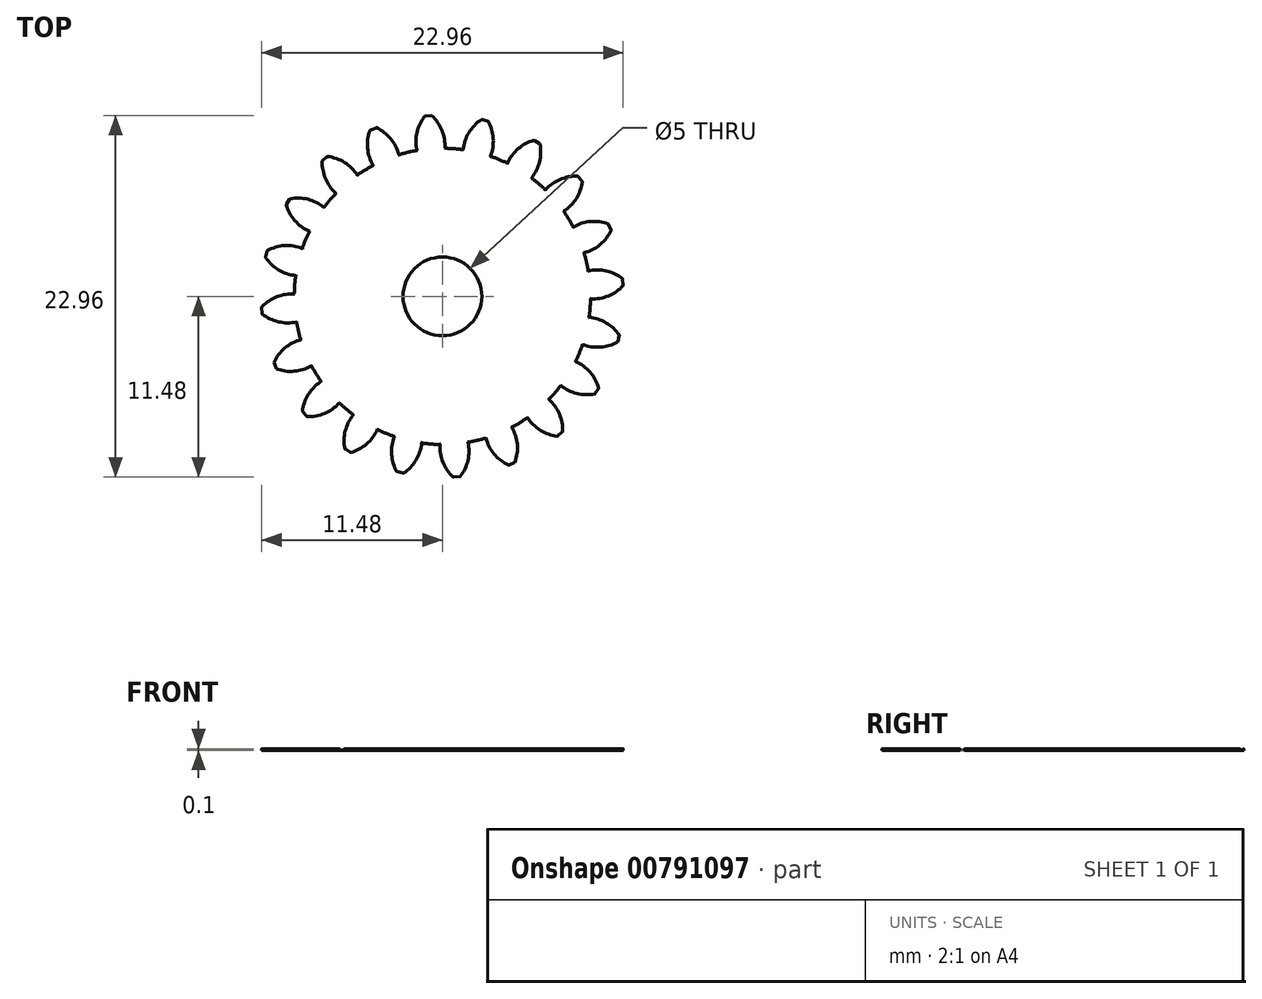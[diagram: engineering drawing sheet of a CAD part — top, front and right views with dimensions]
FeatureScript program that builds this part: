
annotation { "Feature Type Name" : "Feature", "Feature Type Description" : "" }
export const myFeature = defineFeature(function(context is Context, id is Id, definition is map)
    precondition{}
    {
        {
            assignVariable(context, id + "F0", {"name" : "GearDepth", "anyValue" : .1});
        }
        {
            assignVariable(context, id + "F1", {"name" : "TeethFillet", "anyValue" : getVariable(context, 'GearDepth') * .25});
        }
        {
            var Q0;
            Q0=qCreatedBy(makeId("Top.planeOp"),FACE);
            var sketch = newSketch(context, id + "F2", { "sketchPlane" : qUnion([Q0])});
            skCircle(sketch, "E0", {"center": v(0, 0) * mm, "radius": 9.4 * mm});
            skCircle(sketch, "E1", {"center": v(0, 0) * mm, "radius": 10.45 * mm, "construction": true});
            skCircle(sketch, "E2", {"center": v(0, 0) * mm, "radius": 11.5 * mm, "construction": true});
            skLineSegment(sketch, "E3", {"start": v(0, 0) * mm, "end": v(0, 17.6) * mm, "construction": true});
            skLineSegment(sketch, "E4", {"start": v(0, 0) * mm, "end": v(-1.42, 18) * mm, "construction": true});
            skLineSegment(sketch, "E5", {"start": v(0, 10.45) * mm, "end": v(-10.54, 10.45) * mm, "construction": true});
            skLineSegment(sketch, "E6", {"start": v(0, 10.45) * mm, "end": v(-10.3, 6.7) * mm, "construction": true});
            skCircle(sketch, "E7", {"center": v(0, 10.45) * mm, "radius": 2.61 * mm, "construction": true});
            skCircle(sketch, "E8", {"center": v(-2.46, 9.56) * mm, "radius": 2.61 * mm, "construction": true});
            skArc(sketch, "E9", {"start": v(-4.91, 10.45) * mm, "mid": v(-4.92, 10.42) * mm, "end": v(-4.94, 10.39) * mm});
            skArc(sketch, "E10.trimOffspring", {"start": v(0.15, 9.4) * mm, "mid": v(-0.03, 10.54) * mm, "end": v(-0.68, 11.48) * mm});
            skArc(sketch, "E11.MirrorCS", {"start": v(-1.62, 9.27) * mm, "mid": v(-1.62, 10.41) * mm, "end": v(-1.12, 11.45) * mm});
            skLineSegment(sketch, "E12", {"start": v(-1.12, 11.45) * mm, "end": v(-0.68, 11.48) * mm});
            skArc(sketch, "E13.1.0", {"start": v(-2.76, 9) * mm, "mid": v(-3.29, 10.01) * mm, "end": v(-4.2, 10.7) * mm});
            skLineSegment(sketch, "E13.1.1", {"start": v(-4.6, 10.54) * mm, "end": v(-4.2, 10.7) * mm});
            skArc(sketch, "E13.1.2", {"start": v(-4.4, 8.31) * mm, "mid": v(-4.76, 9.4) * mm, "end": v(-4.6, 10.54) * mm});
            skArc(sketch, "E13.2.0", {"start": v(-5.4, 7.7) * mm, "mid": v(-6.22, 8.5) * mm, "end": v(-7.3, 8.89) * mm});
            skLineSegment(sketch, "E13.2.1", {"start": v(-7.64, 8.6) * mm, "end": v(-7.3, 8.89) * mm});
            skArc(sketch, "E13.2.2", {"start": v(-6.76, 6.54) * mm, "mid": v(-7.43, 7.47) * mm, "end": v(-7.64, 8.6) * mm});
            skArc(sketch, "E13.3.0", {"start": v(-7.52, 5.65) * mm, "mid": v(-8.54, 6.17) * mm, "end": v(-9.69, 6.2) * mm});
            skLineSegment(sketch, "E13.3.1", {"start": v(-9.92, 5.82) * mm, "end": v(-9.69, 6.2) * mm});
            skArc(sketch, "E13.3.2", {"start": v(-8.45, 4.13) * mm, "mid": v(-9.37, 4.81) * mm, "end": v(-9.92, 5.82) * mm});
            skArc(sketch, "E13.4.0", {"start": v(-8.9, 3.05) * mm, "mid": v(-10.03, 3.23) * mm, "end": v(-11.13, 2.9) * mm});
            skLineSegment(sketch, "E13.4.1", {"start": v(-11.23, 2.47) * mm, "end": v(-11.13, 2.9) * mm});
            skArc(sketch, "E13.4.2", {"start": v(-9.32, 1.32) * mm, "mid": v(-10.4, 1.68) * mm, "end": v(-11.23, 2.47) * mm});
            skArc(sketch, "E13.5.0", {"start": v(-9.4, 0.15) * mm, "mid": v(-10.54, -0.03) * mm, "end": v(-11.48, -0.68) * mm});
            skLineSegment(sketch, "E13.5.1", {"start": v(-11.45, -1.12) * mm, "end": v(-11.48, -0.68) * mm});
            skArc(sketch, "E13.5.2", {"start": v(-9.27, -1.62) * mm, "mid": v(-10.41, -1.62) * mm, "end": v(-11.45, -1.12) * mm});
            skArc(sketch, "E13.6.0", {"start": v(-9, -2.76) * mm, "mid": v(-10.01, -3.29) * mm, "end": v(-10.7, -4.2) * mm});
            skLineSegment(sketch, "E13.6.1", {"start": v(-10.54, -4.6) * mm, "end": v(-10.7, -4.2) * mm});
            skArc(sketch, "E13.6.2", {"start": v(-8.31, -4.4) * mm, "mid": v(-9.4, -4.76) * mm, "end": v(-10.54, -4.6) * mm});
            skArc(sketch, "E13.7.0", {"start": v(-7.7, -5.4) * mm, "mid": v(-8.5, -6.22) * mm, "end": v(-8.89, -7.3) * mm});
            skLineSegment(sketch, "E13.7.1", {"start": v(-8.6, -7.64) * mm, "end": v(-8.89, -7.3) * mm});
            skArc(sketch, "E13.7.2", {"start": v(-6.54, -6.76) * mm, "mid": v(-7.47, -7.43) * mm, "end": v(-8.6, -7.64) * mm});
            skArc(sketch, "E13.8.0", {"start": v(-5.65, -7.52) * mm, "mid": v(-6.17, -8.54) * mm, "end": v(-6.2, -9.69) * mm});
            skLineSegment(sketch, "E13.8.1", {"start": v(-5.82, -9.92) * mm, "end": v(-6.2, -9.69) * mm});
            skArc(sketch, "E13.8.2", {"start": v(-4.13, -8.45) * mm, "mid": v(-4.81, -9.37) * mm, "end": v(-5.82, -9.92) * mm});
            skArc(sketch, "E13.9.0", {"start": v(-3.05, -8.9) * mm, "mid": v(-3.23, -10.03) * mm, "end": v(-2.9, -11.13) * mm});
            skLineSegment(sketch, "E13.9.1", {"start": v(-2.47, -11.23) * mm, "end": v(-2.9, -11.13) * mm});
            skArc(sketch, "E13.9.2", {"start": v(-1.32, -9.32) * mm, "mid": v(-1.68, -10.4) * mm, "end": v(-2.47, -11.23) * mm});
            skArc(sketch, "E13.10.0", {"start": v(-0.15, -9.4) * mm, "mid": v(0.03, -10.54) * mm, "end": v(0.68, -11.48) * mm});
            skLineSegment(sketch, "E13.10.1", {"start": v(1.12, -11.45) * mm, "end": v(0.68, -11.48) * mm});
            skArc(sketch, "E13.10.2", {"start": v(1.62, -9.27) * mm, "mid": v(1.62, -10.41) * mm, "end": v(1.12, -11.45) * mm});
            skArc(sketch, "E13.11.0", {"start": v(2.76, -9) * mm, "mid": v(3.29, -10.01) * mm, "end": v(4.2, -10.7) * mm});
            skLineSegment(sketch, "E13.11.1", {"start": v(4.6, -10.54) * mm, "end": v(4.2, -10.7) * mm});
            skArc(sketch, "E13.11.2", {"start": v(4.4, -8.31) * mm, "mid": v(4.76, -9.4) * mm, "end": v(4.6, -10.54) * mm});
            skArc(sketch, "E13.12.0", {"start": v(5.4, -7.7) * mm, "mid": v(6.22, -8.5) * mm, "end": v(7.3, -8.89) * mm});
            skLineSegment(sketch, "E13.12.1", {"start": v(7.64, -8.6) * mm, "end": v(7.3, -8.89) * mm});
            skArc(sketch, "E13.12.2", {"start": v(6.76, -6.54) * mm, "mid": v(7.43, -7.47) * mm, "end": v(7.64, -8.6) * mm});
            skArc(sketch, "E13.13.0", {"start": v(7.52, -5.65) * mm, "mid": v(8.54, -6.17) * mm, "end": v(9.69, -6.2) * mm});
            skLineSegment(sketch, "E13.13.1", {"start": v(9.92, -5.82) * mm, "end": v(9.69, -6.2) * mm});
            skArc(sketch, "E13.13.2", {"start": v(8.45, -4.13) * mm, "mid": v(9.37, -4.81) * mm, "end": v(9.92, -5.82) * mm});
            skArc(sketch, "E13.14.0", {"start": v(8.9, -3.05) * mm, "mid": v(10.03, -3.23) * mm, "end": v(11.13, -2.9) * mm});
            skLineSegment(sketch, "E13.14.1", {"start": v(11.23, -2.47) * mm, "end": v(11.13, -2.9) * mm});
            skArc(sketch, "E13.14.2", {"start": v(9.32, -1.32) * mm, "mid": v(10.4, -1.68) * mm, "end": v(11.23, -2.47) * mm});
            skArc(sketch, "E13.15.0", {"start": v(9.4, -0.15) * mm, "mid": v(10.54, 0.03) * mm, "end": v(11.48, 0.68) * mm});
            skLineSegment(sketch, "E13.15.1", {"start": v(11.45, 1.12) * mm, "end": v(11.48, 0.68) * mm});
            skArc(sketch, "E13.15.2", {"start": v(9.27, 1.62) * mm, "mid": v(10.41, 1.62) * mm, "end": v(11.45, 1.12) * mm});
            skArc(sketch, "E13.16.0", {"start": v(9, 2.76) * mm, "mid": v(10.01, 3.29) * mm, "end": v(10.7, 4.2) * mm});
            skLineSegment(sketch, "E13.16.1", {"start": v(10.54, 4.6) * mm, "end": v(10.7, 4.2) * mm});
            skArc(sketch, "E13.16.2", {"start": v(8.31, 4.4) * mm, "mid": v(9.4, 4.76) * mm, "end": v(10.54, 4.6) * mm});
            skArc(sketch, "E13.17.0", {"start": v(7.7, 5.4) * mm, "mid": v(8.5, 6.22) * mm, "end": v(8.89, 7.3) * mm});
            skLineSegment(sketch, "E13.17.1", {"start": v(8.6, 7.64) * mm, "end": v(8.89, 7.3) * mm});
            skArc(sketch, "E13.17.2", {"start": v(6.54, 6.76) * mm, "mid": v(7.47, 7.43) * mm, "end": v(8.6, 7.64) * mm});
            skArc(sketch, "E13.18.0", {"start": v(5.65, 7.52) * mm, "mid": v(6.17, 8.54) * mm, "end": v(6.2, 9.69) * mm});
            skLineSegment(sketch, "E13.18.1", {"start": v(5.82, 9.92) * mm, "end": v(6.2, 9.69) * mm});
            skArc(sketch, "E13.18.2", {"start": v(4.13, 8.45) * mm, "mid": v(4.81, 9.37) * mm, "end": v(5.82, 9.92) * mm});
            skArc(sketch, "E13.19.0", {"start": v(3.05, 8.9) * mm, "mid": v(3.23, 10.03) * mm, "end": v(2.9, 11.13) * mm});
            skLineSegment(sketch, "E13.19.1", {"start": v(2.47, 11.23) * mm, "end": v(2.9, 11.13) * mm});
            skArc(sketch, "E13.19.2", {"start": v(1.32, 9.32) * mm, "mid": v(1.68, 10.4) * mm, "end": v(2.47, 11.23) * mm});
            skCircle(sketch, "E14", {"center": v(0, 0) * mm, "radius": 2.5 * mm});
            skSolve(sketch);
        }
        {
            var Q0;
            {var subQ0=sQuery(id+"F2.wireOp",EDGE,"E10.trimOffspring");Q0=makeQuery(id+"F2.imprint","IMPRINT",FACE,{"disambiguationData":[TD([[makeQuery(id+"F2.imprint","IMPRINT",EDGE,{"derivedFrom":subQ0}),1.0]])]});}
            var Q1;
            {var subQ0=sQuery(id+"F2.wireOp",EDGE,"E0");var subQ1=makeQuery(id+"F2.imprint","INTERSECT",VERTEX,{"derivedFrom":[subQ0,sQuery(id+"F2.wireOp",EDGE,"E10.trimOffspring")]});Q1=makeQuery(id+"F2.imprint","IMPRINT",FACE,{"disambiguationData":[TD([[makeQuery(id+"F2.imprint","IMPRINT",EDGE,{"disambiguationData":[TD([[subQ1,-1.0]])],"derivedFrom":subQ0}),1.0]])]});}
            var Q2;
            {var subQ0=sQuery(id+"F2.wireOp",EDGE,"E13.1.0");Q2=makeQuery(id+"F2.imprint","IMPRINT",FACE,{"disambiguationData":[TD([[makeQuery(id+"F2.imprint","IMPRINT",EDGE,{"derivedFrom":subQ0}),1.0]])]});}
            var Q3;
            {var subQ0=sQuery(id+"F2.wireOp",EDGE,"E13.2.0");Q3=makeQuery(id+"F2.imprint","IMPRINT",FACE,{"disambiguationData":[TD([[makeQuery(id+"F2.imprint","IMPRINT",EDGE,{"derivedFrom":subQ0}),1.0]])]});}
            var Q4;
            {var subQ0=sQuery(id+"F2.wireOp",EDGE,"E13.3.0");Q4=makeQuery(id+"F2.imprint","IMPRINT",FACE,{"disambiguationData":[TD([[makeQuery(id+"F2.imprint","IMPRINT",EDGE,{"derivedFrom":subQ0}),1.0]])]});}
            var Q5;
            {var subQ0=sQuery(id+"F2.wireOp",EDGE,"E13.4.0");Q5=makeQuery(id+"F2.imprint","IMPRINT",FACE,{"disambiguationData":[TD([[makeQuery(id+"F2.imprint","IMPRINT",EDGE,{"derivedFrom":subQ0}),1.0]])]});}
            var Q6;
            {var subQ0=sQuery(id+"F2.wireOp",EDGE,"E13.5.0");Q6=makeQuery(id+"F2.imprint","IMPRINT",FACE,{"disambiguationData":[TD([[makeQuery(id+"F2.imprint","IMPRINT",EDGE,{"derivedFrom":subQ0}),1.0]])]});}
            var Q7;
            {var subQ0=sQuery(id+"F2.wireOp",EDGE,"E13.6.0");Q7=makeQuery(id+"F2.imprint","IMPRINT",FACE,{"disambiguationData":[TD([[makeQuery(id+"F2.imprint","IMPRINT",EDGE,{"derivedFrom":subQ0}),1.0]])]});}
            var Q8;
            {var subQ0=sQuery(id+"F2.wireOp",EDGE,"E13.7.0");Q8=makeQuery(id+"F2.imprint","IMPRINT",FACE,{"disambiguationData":[TD([[makeQuery(id+"F2.imprint","IMPRINT",EDGE,{"derivedFrom":subQ0}),1.0]])]});}
            var Q9;
            {var subQ0=sQuery(id+"F2.wireOp",EDGE,"E13.8.0");Q9=makeQuery(id+"F2.imprint","IMPRINT",FACE,{"disambiguationData":[TD([[makeQuery(id+"F2.imprint","IMPRINT",EDGE,{"derivedFrom":subQ0}),1.0]])]});}
            var Q10;
            {var subQ0=sQuery(id+"F2.wireOp",EDGE,"E13.9.0");Q10=makeQuery(id+"F2.imprint","IMPRINT",FACE,{"disambiguationData":[TD([[makeQuery(id+"F2.imprint","IMPRINT",EDGE,{"derivedFrom":subQ0}),1.0]])]});}
            var Q11;
            {var subQ0=sQuery(id+"F2.wireOp",EDGE,"E13.10.0");Q11=makeQuery(id+"F2.imprint","IMPRINT",FACE,{"disambiguationData":[TD([[makeQuery(id+"F2.imprint","IMPRINT",EDGE,{"derivedFrom":subQ0}),1.0]])]});}
            var Q12;
            {var subQ0=sQuery(id+"F2.wireOp",EDGE,"E13.11.0");Q12=makeQuery(id+"F2.imprint","IMPRINT",FACE,{"disambiguationData":[TD([[makeQuery(id+"F2.imprint","IMPRINT",EDGE,{"derivedFrom":subQ0}),1.0]])]});}
            var Q13;
            {var subQ0=sQuery(id+"F2.wireOp",EDGE,"E13.12.0");Q13=makeQuery(id+"F2.imprint","IMPRINT",FACE,{"disambiguationData":[TD([[makeQuery(id+"F2.imprint","IMPRINT",EDGE,{"derivedFrom":subQ0}),1.0]])]});}
            var Q14;
            {var subQ0=sQuery(id+"F2.wireOp",EDGE,"E13.13.0");Q14=makeQuery(id+"F2.imprint","IMPRINT",FACE,{"disambiguationData":[TD([[makeQuery(id+"F2.imprint","IMPRINT",EDGE,{"derivedFrom":subQ0}),1.0]])]});}
            var Q15;
            {var subQ0=sQuery(id+"F2.wireOp",EDGE,"E13.14.0");Q15=makeQuery(id+"F2.imprint","IMPRINT",FACE,{"disambiguationData":[TD([[makeQuery(id+"F2.imprint","IMPRINT",EDGE,{"derivedFrom":subQ0}),1.0]])]});}
            var Q16;
            {var subQ0=sQuery(id+"F2.wireOp",EDGE,"E13.15.0");Q16=makeQuery(id+"F2.imprint","IMPRINT",FACE,{"disambiguationData":[TD([[makeQuery(id+"F2.imprint","IMPRINT",EDGE,{"derivedFrom":subQ0}),1.0]])]});}
            var Q17;
            {var subQ0=sQuery(id+"F2.wireOp",EDGE,"E13.16.0");Q17=makeQuery(id+"F2.imprint","IMPRINT",FACE,{"disambiguationData":[TD([[makeQuery(id+"F2.imprint","IMPRINT",EDGE,{"derivedFrom":subQ0}),1.0]])]});}
            var Q18;
            {var subQ0=sQuery(id+"F2.wireOp",EDGE,"E13.17.0");Q18=makeQuery(id+"F2.imprint","IMPRINT",FACE,{"disambiguationData":[TD([[makeQuery(id+"F2.imprint","IMPRINT",EDGE,{"derivedFrom":subQ0}),1.0]])]});}
            var Q19;
            {var subQ0=sQuery(id+"F2.wireOp",EDGE,"E13.18.0");Q19=makeQuery(id+"F2.imprint","IMPRINT",FACE,{"disambiguationData":[TD([[makeQuery(id+"F2.imprint","IMPRINT",EDGE,{"derivedFrom":subQ0}),1.0]])]});}
            var Q20;
            {var subQ0=sQuery(id+"F2.wireOp",EDGE,"E13.19.0");Q20=makeQuery(id+"F2.imprint","IMPRINT",FACE,{"disambiguationData":[TD([[makeQuery(id+"F2.imprint","IMPRINT",EDGE,{"derivedFrom":subQ0}),1.0]])]});}
            var Q21;
            Q21=sQuery(id+"F2.wireOp",EDGE,"E0");
            var Q22;
            Q22=sQuery(id+"F2.wireOp",EDGE,"E10.trimOffspring");
            var Q23;
            Q23=sQuery(id+"F2.wireOp",EDGE,"E12");
            var Q24;
            Q24=sQuery(id+"F2.wireOp",EDGE,"E11.MirrorCS");
            extrude(context, id + "F3", {"entities" : qUnion([Q0, Q1, Q2, Q3, Q4, Q5, Q6, Q7, Q8, Q9, Q10, Q11, Q12, Q13, Q14, Q15, Q16, Q17, Q18, Q19, Q20]), "surfaceEntities" : qUnion([Q21, Q22, Q23, Q24]), "depth" : (getVariable(context, 'GearDepth')) * mm});
        }
        {
            var Q0;
            Q0=makeQuery(id+"F3.opExtrude","CAP_EDGE",EDGE,{"disambiguationData":[OSD([sQuery(id+"F2.wireOp",EDGE,"E13.5.2")])],"isStart":false});
            var Q1;
            Q1=makeQuery(id+"F3.opExtrude","CAP_EDGE",EDGE,{"disambiguationData":[OSD([sQuery(id+"F2.wireOp",EDGE,"E13.5.1")])],"isStart":false});
            var Q2;
            {var subQ0=sQuery(id+"F2.wireOp",EDGE,"E0");Q2=makeQuery(id+"F3.opExtrude","CAP_EDGE",EDGE,{"disambiguationData":[OSD([subQ0]),TDD([makeQuery(id+"F2.imprint","IMPRINT",EDGE,{"disambiguationData":[TD([[makeQuery(id+"F2.imprint","INTERSECT",VERTEX,{"derivedFrom":[subQ0,sQuery(id+"F2.wireOp",EDGE,"E13.5.2")]}),-1.0]])],"derivedFrom":subQ0})])],"isStart":false});}
            var Q3;
            Q3=makeQuery(id+"F3.opExtrude","CAP_EDGE",EDGE,{"disambiguationData":[OSD([sQuery(id+"F2.wireOp",EDGE,"E13.6.0")])],"isStart":false});
            var Q4;
            Q4=makeQuery(id+"F3.opExtrude","CAP_EDGE",EDGE,{"disambiguationData":[OSD([sQuery(id+"F2.wireOp",EDGE,"E13.6.1")])],"isStart":false});
            var Q5;
            Q5=makeQuery(id+"F3.opExtrude","CAP_EDGE",EDGE,{"disambiguationData":[OSD([sQuery(id+"F2.wireOp",EDGE,"E13.6.2")])],"isStart":false});
            var Q6;
            {var subQ0=sQuery(id+"F2.wireOp",EDGE,"E0");Q6=makeQuery(id+"F3.opExtrude","SWEPT_FACE",FACE,{"disambiguationData":[OSD([subQ0]),TDD([makeQuery(id+"F2.imprint","IMPRINT",EDGE,{"disambiguationData":[TD([[makeQuery(id+"F2.imprint","INTERSECT",VERTEX,{"derivedFrom":[subQ0,sQuery(id+"F2.wireOp",EDGE,"E13.6.2")]}),-1.0]])],"derivedFrom":subQ0})])]});}
            var Q7;
            {var subQ0=sQuery(id+"F2.wireOp",EDGE,"E0");Q7=makeQuery(id+"F3.opExtrude","CAP_EDGE",EDGE,{"disambiguationData":[OSD([subQ0]),TDD([makeQuery(id+"F2.imprint","IMPRINT",EDGE,{"disambiguationData":[TD([[makeQuery(id+"F2.imprint","INTERSECT",VERTEX,{"derivedFrom":[subQ0,sQuery(id+"F2.wireOp",EDGE,"E13.6.2")]}),-1.0]])],"derivedFrom":subQ0})])],"isStart":false});}
            var Q8;
            Q8=makeQuery(id+"F3.opExtrude","CAP_EDGE",EDGE,{"disambiguationData":[OSD([sQuery(id+"F2.wireOp",EDGE,"E13.7.2")])],"isStart":true});
            var Q9;
            {var subQ0=sQuery(id+"F2.wireOp",EDGE,"E0");Q9=makeQuery(id+"F3.opExtrude","CAP_EDGE",EDGE,{"disambiguationData":[OSD([subQ0]),TDD([makeQuery(id+"F2.imprint","IMPRINT",EDGE,{"disambiguationData":[TD([[makeQuery(id+"F2.imprint","INTERSECT",VERTEX,{"derivedFrom":[subQ0,sQuery(id+"F2.wireOp",EDGE,"E13.7.2")]}),-1.0]])],"derivedFrom":subQ0})])],"isStart":true});}
            var Q10;
            Q10=makeQuery(id+"F3.opExtrude","CAP_EDGE",EDGE,{"disambiguationData":[OSD([sQuery(id+"F2.wireOp",EDGE,"E13.7.2")])],"isStart":false});
            var Q11;
            {var subQ0=sQuery(id+"F2.wireOp",EDGE,"E0");Q11=makeQuery(id+"F3.opExtrude","CAP_EDGE",EDGE,{"disambiguationData":[OSD([subQ0]),TDD([makeQuery(id+"F2.imprint","IMPRINT",EDGE,{"disambiguationData":[TD([[makeQuery(id+"F2.imprint","INTERSECT",VERTEX,{"derivedFrom":[subQ0,sQuery(id+"F2.wireOp",EDGE,"E13.7.2")]}),-1.0]])],"derivedFrom":subQ0})])],"isStart":false});}
            var Q12;
            Q12=makeQuery(id+"F3.opExtrude","CAP_EDGE",EDGE,{"disambiguationData":[OSD([sQuery(id+"F2.wireOp",EDGE,"E13.8.0")])],"isStart":false});
            var Q13;
            {var subQ0=sQuery(id+"F2.wireOp",EDGE,"E0");Q13=makeQuery(id+"F3.opExtrude","SWEPT_FACE",FACE,{"disambiguationData":[OSD([subQ0]),TDD([makeQuery(id+"F2.imprint","IMPRINT",EDGE,{"disambiguationData":[TD([[makeQuery(id+"F2.imprint","INTERSECT",VERTEX,{"derivedFrom":[subQ0,sQuery(id+"F2.wireOp",EDGE,"E13.7.2")]}),-1.0]])],"derivedFrom":subQ0})])]});}
            var Q14;
            Q14=makeQuery(id+"F3.opExtrude","CAP_EDGE",EDGE,{"disambiguationData":[OSD([sQuery(id+"F2.wireOp",EDGE,"E13.6.0")])],"isStart":true});
            var Q15;
            Q15=makeQuery(id+"F3.opExtrude","CAP_EDGE",EDGE,{"disambiguationData":[OSD([sQuery(id+"F2.wireOp",EDGE,"E13.8.2")])],"isStart":false});
            var Q16;
            {var subQ0=sQuery(id+"F2.wireOp",EDGE,"E0");Q16=makeQuery(id+"F3.opExtrude","CAP_EDGE",EDGE,{"disambiguationData":[OSD([subQ0]),TDD([makeQuery(id+"F2.imprint","IMPRINT",EDGE,{"disambiguationData":[TD([[makeQuery(id+"F2.imprint","INTERSECT",VERTEX,{"derivedFrom":[subQ0,sQuery(id+"F2.wireOp",EDGE,"E13.8.2")]}),-1.0]])],"derivedFrom":subQ0})])],"isStart":false});}
            var Q17;
            Q17=makeQuery(id+"F3.opExtrude","CAP_EDGE",EDGE,{"disambiguationData":[OSD([sQuery(id+"F2.wireOp",EDGE,"E13.9.0")])],"isStart":false});
            var Q18;
            Q18=makeQuery(id+"F3.opExtrude","CAP_EDGE",EDGE,{"disambiguationData":[OSD([sQuery(id+"F2.wireOp",EDGE,"E13.9.2")])],"isStart":false});
            var Q19;
            {var subQ0=sQuery(id+"F2.wireOp",EDGE,"E0");Q19=makeQuery(id+"F3.opExtrude","CAP_EDGE",EDGE,{"disambiguationData":[OSD([subQ0]),TDD([makeQuery(id+"F2.imprint","IMPRINT",EDGE,{"disambiguationData":[TD([[makeQuery(id+"F2.imprint","INTERSECT",VERTEX,{"derivedFrom":[subQ0,sQuery(id+"F2.wireOp",EDGE,"E13.9.2")]}),-1.0]])],"derivedFrom":subQ0})])],"isStart":false});}
            var Q20;
            Q20=makeQuery(id+"F3.opExtrude","CAP_EDGE",EDGE,{"disambiguationData":[OSD([sQuery(id+"F2.wireOp",EDGE,"E13.10.0")])],"isStart":false});
            var Q21;
            Q21=makeQuery(id+"F3.opExtrude","CAP_EDGE",EDGE,{"disambiguationData":[OSD([sQuery(id+"F2.wireOp",EDGE,"E13.10.2")])],"isStart":false});
            var Q22;
            {var subQ0=sQuery(id+"F2.wireOp",EDGE,"E0");Q22=makeQuery(id+"F3.opExtrude","CAP_EDGE",EDGE,{"disambiguationData":[OSD([subQ0]),TDD([makeQuery(id+"F2.imprint","IMPRINT",EDGE,{"disambiguationData":[TD([[makeQuery(id+"F2.imprint","INTERSECT",VERTEX,{"derivedFrom":[subQ0,sQuery(id+"F2.wireOp",EDGE,"E13.10.2")]}),-1.0]])],"derivedFrom":subQ0})])],"isStart":false});}
            var Q23;
            Q23=makeQuery(id+"F3.opExtrude","CAP_EDGE",EDGE,{"disambiguationData":[OSD([sQuery(id+"F2.wireOp",EDGE,"E13.11.0")])],"isStart":false});
            var Q24;
            Q24=makeQuery(id+"F3.opExtrude","CAP_EDGE",EDGE,{"disambiguationData":[OSD([sQuery(id+"F2.wireOp",EDGE,"E13.11.2")])],"isStart":false});
            var Q25;
            {var subQ0=sQuery(id+"F2.wireOp",EDGE,"E0");Q25=makeQuery(id+"F3.opExtrude","CAP_EDGE",EDGE,{"disambiguationData":[OSD([subQ0]),TDD([makeQuery(id+"F2.imprint","IMPRINT",EDGE,{"disambiguationData":[TD([[makeQuery(id+"F2.imprint","INTERSECT",VERTEX,{"derivedFrom":[subQ0,sQuery(id+"F2.wireOp",EDGE,"E13.11.2")]}),-1.0]])],"derivedFrom":subQ0})])],"isStart":false});}
            var Q26;
            Q26=makeQuery(id+"F3.opExtrude","CAP_EDGE",EDGE,{"disambiguationData":[OSD([sQuery(id+"F2.wireOp",EDGE,"E13.12.0")])],"isStart":false});
            var Q27;
            Q27=makeQuery(id+"F3.opExtrude","CAP_EDGE",EDGE,{"disambiguationData":[OSD([sQuery(id+"F2.wireOp",EDGE,"E13.12.2")])],"isStart":false});
            var Q28;
            {var subQ0=sQuery(id+"F2.wireOp",EDGE,"E0");Q28=makeQuery(id+"F3.opExtrude","CAP_EDGE",EDGE,{"disambiguationData":[OSD([subQ0]),TDD([makeQuery(id+"F2.imprint","IMPRINT",EDGE,{"disambiguationData":[TD([[makeQuery(id+"F2.imprint","INTERSECT",VERTEX,{"derivedFrom":[subQ0,sQuery(id+"F2.wireOp",EDGE,"E13.12.2")]}),-1.0]])],"derivedFrom":subQ0})])],"isStart":false});}
            var Q29;
            Q29=makeQuery(id+"F3.opExtrude","CAP_EDGE",EDGE,{"disambiguationData":[OSD([sQuery(id+"F2.wireOp",EDGE,"E13.13.0")])],"isStart":false});
            var Q30;
            Q30=makeQuery(id+"F3.opExtrude","CAP_EDGE",EDGE,{"disambiguationData":[OSD([sQuery(id+"F2.wireOp",EDGE,"E13.13.2")])],"isStart":false});
            var Q31;
            {var subQ0=sQuery(id+"F2.wireOp",EDGE,"E0");Q31=makeQuery(id+"F3.opExtrude","CAP_EDGE",EDGE,{"disambiguationData":[OSD([subQ0]),TDD([makeQuery(id+"F2.imprint","IMPRINT",EDGE,{"disambiguationData":[TD([[makeQuery(id+"F2.imprint","INTERSECT",VERTEX,{"derivedFrom":[subQ0,sQuery(id+"F2.wireOp",EDGE,"E13.13.2")]}),-1.0]])],"derivedFrom":subQ0})])],"isStart":false});}
            var Q32;
            Q32=makeQuery(id+"F3.opExtrude","CAP_EDGE",EDGE,{"disambiguationData":[OSD([sQuery(id+"F2.wireOp",EDGE,"E13.14.0")])],"isStart":false});
            var Q33;
            Q33=makeQuery(id+"F3.opExtrude","CAP_EDGE",EDGE,{"disambiguationData":[OSD([sQuery(id+"F2.wireOp",EDGE,"E13.14.2")])],"isStart":false});
            var Q34;
            {var subQ0=sQuery(id+"F2.wireOp",EDGE,"E0");Q34=makeQuery(id+"F3.opExtrude","CAP_EDGE",EDGE,{"disambiguationData":[OSD([subQ0]),TDD([makeQuery(id+"F2.imprint","IMPRINT",EDGE,{"disambiguationData":[TD([[makeQuery(id+"F2.imprint","INTERSECT",VERTEX,{"derivedFrom":[subQ0,sQuery(id+"F2.wireOp",EDGE,"E13.14.2")]}),-1.0]])],"derivedFrom":subQ0})])],"isStart":false});}
            var Q35;
            Q35=makeQuery(id+"F3.opExtrude","CAP_EDGE",EDGE,{"disambiguationData":[OSD([sQuery(id+"F2.wireOp",EDGE,"E13.15.0")])],"isStart":false});
            var Q36;
            {var subQ0=sQuery(id+"F2.wireOp",EDGE,"E0");Q36=makeQuery(id+"F3.opExtrude","CAP_EDGE",EDGE,{"disambiguationData":[OSD([subQ0]),TDD([makeQuery(id+"F2.imprint","IMPRINT",EDGE,{"disambiguationData":[TD([[makeQuery(id+"F2.imprint","INTERSECT",VERTEX,{"derivedFrom":[subQ0,sQuery(id+"F2.wireOp",EDGE,"E13.14.2")]}),-1.0]])],"derivedFrom":subQ0})])],"isStart":false});}
            var Q37;
            Q37=makeQuery(id+"F3.opExtrude","CAP_EDGE",EDGE,{"disambiguationData":[OSD([sQuery(id+"F2.wireOp",EDGE,"E13.15.2")])],"isStart":false});
            var Q38;
            {var subQ0=sQuery(id+"F2.wireOp",EDGE,"E0");Q38=makeQuery(id+"F3.opExtrude","CAP_EDGE",EDGE,{"disambiguationData":[OSD([subQ0]),TDD([makeQuery(id+"F2.imprint","IMPRINT",EDGE,{"disambiguationData":[TD([[makeQuery(id+"F2.imprint","INTERSECT",VERTEX,{"derivedFrom":[subQ0,sQuery(id+"F2.wireOp",EDGE,"E13.15.2")]}),-1.0]])],"derivedFrom":subQ0})])],"isStart":false});}
            var Q39;
            Q39=makeQuery(id+"F3.opExtrude","CAP_EDGE",EDGE,{"disambiguationData":[OSD([sQuery(id+"F2.wireOp",EDGE,"E13.16.0")])],"isStart":false});
            var Q40;
            Q40=makeQuery(id+"F3.opExtrude","CAP_EDGE",EDGE,{"disambiguationData":[OSD([sQuery(id+"F2.wireOp",EDGE,"E13.16.2")])],"isStart":false});
            var Q41;
            Q41=makeQuery(id+"F3.opExtrude","CAP_EDGE",EDGE,{"disambiguationData":[OSD([sQuery(id+"F2.wireOp",EDGE,"E13.17.0")])],"isStart":false});
            var Q42;
            {var subQ0=sQuery(id+"F2.wireOp",EDGE,"E0");Q42=makeQuery(id+"F3.opExtrude","CAP_EDGE",EDGE,{"disambiguationData":[OSD([subQ0]),TDD([makeQuery(id+"F2.imprint","IMPRINT",EDGE,{"disambiguationData":[TD([[makeQuery(id+"F2.imprint","INTERSECT",VERTEX,{"derivedFrom":[subQ0,sQuery(id+"F2.wireOp",EDGE,"E13.16.2")]}),-1.0]])],"derivedFrom":subQ0})])],"isStart":false});}
            var Q43;
            Q43=makeQuery(id+"F3.opExtrude","CAP_EDGE",EDGE,{"disambiguationData":[OSD([sQuery(id+"F2.wireOp",EDGE,"E13.17.2")])],"isStart":false});
            var Q44;
            {var subQ0=sQuery(id+"F2.wireOp",EDGE,"E0");Q44=makeQuery(id+"F3.opExtrude","CAP_EDGE",EDGE,{"disambiguationData":[OSD([subQ0]),TDD([makeQuery(id+"F2.imprint","IMPRINT",EDGE,{"disambiguationData":[TD([[makeQuery(id+"F2.imprint","INTERSECT",VERTEX,{"derivedFrom":[subQ0,sQuery(id+"F2.wireOp",EDGE,"E13.17.2")]}),-1.0]])],"derivedFrom":subQ0})])],"isStart":false});}
            var Q45;
            Q45=makeQuery(id+"F3.opExtrude","CAP_EDGE",EDGE,{"disambiguationData":[OSD([sQuery(id+"F2.wireOp",EDGE,"E13.18.0")])],"isStart":false});
            var Q46;
            Q46=makeQuery(id+"F3.opExtrude","CAP_EDGE",EDGE,{"disambiguationData":[OSD([sQuery(id+"F2.wireOp",EDGE,"E13.18.2")])],"isStart":false});
            var Q47;
            {var subQ0=sQuery(id+"F2.wireOp",EDGE,"E0");Q47=makeQuery(id+"F3.opExtrude","CAP_EDGE",EDGE,{"disambiguationData":[OSD([subQ0]),TDD([makeQuery(id+"F2.imprint","IMPRINT",EDGE,{"disambiguationData":[TD([[makeQuery(id+"F2.imprint","INTERSECT",VERTEX,{"derivedFrom":[subQ0,sQuery(id+"F2.wireOp",EDGE,"E13.18.2")]}),-1.0]])],"derivedFrom":subQ0})])],"isStart":false});}
            var Q48;
            Q48=makeQuery(id+"F3.opExtrude","CAP_EDGE",EDGE,{"disambiguationData":[OSD([sQuery(id+"F2.wireOp",EDGE,"E13.19.0")])],"isStart":false});
            var Q49;
            Q49=makeQuery(id+"F3.opExtrude","CAP_EDGE",EDGE,{"disambiguationData":[OSD([sQuery(id+"F2.wireOp",EDGE,"E13.19.2")])],"isStart":false});
            var Q50;
            Q50=makeQuery(id+"F3.opExtrude","CAP_EDGE",EDGE,{"disambiguationData":[OSD([sQuery(id+"F2.wireOp",EDGE,"E10.trimOffspring")])],"isStart":false});
            var Q51;
            Q51=makeQuery(id+"F3.opExtrude","CAP_EDGE",EDGE,{"disambiguationData":[OSD([sQuery(id+"F2.wireOp",EDGE,"E11.MirrorCS")])],"isStart":false});
            var Q52;
            {var subQ0=sQuery(id+"F2.wireOp",EDGE,"E0");Q52=makeQuery(id+"F3.opExtrude","CAP_EDGE",EDGE,{"disambiguationData":[OSD([subQ0]),TDD([makeQuery(id+"F2.imprint","IMPRINT",EDGE,{"disambiguationData":[TD([[makeQuery(id+"F2.imprint","INTERSECT",VERTEX,{"derivedFrom":[subQ0,sQuery(id+"F2.wireOp",EDGE,"E11.MirrorCS")]}),-1.0]])],"derivedFrom":subQ0})])],"isStart":false});}
            var Q53;
            Q53=makeQuery(id+"F3.opExtrude","CAP_EDGE",EDGE,{"disambiguationData":[OSD([sQuery(id+"F2.wireOp",EDGE,"E13.1.0")])],"isStart":false});
            var Q54;
            Q54=makeQuery(id+"F3.opExtrude","CAP_EDGE",EDGE,{"disambiguationData":[OSD([sQuery(id+"F2.wireOp",EDGE,"E13.1.2")])],"isStart":false});
            var Q55;
            {var subQ0=sQuery(id+"F2.wireOp",EDGE,"E0");Q55=makeQuery(id+"F3.opExtrude","CAP_EDGE",EDGE,{"disambiguationData":[OSD([subQ0]),TDD([makeQuery(id+"F2.imprint","IMPRINT",EDGE,{"disambiguationData":[TD([[makeQuery(id+"F2.imprint","INTERSECT",VERTEX,{"derivedFrom":[subQ0,sQuery(id+"F2.wireOp",EDGE,"E13.1.2")]}),-1.0]])],"derivedFrom":subQ0})])],"isStart":false});}
            var Q56;
            Q56=makeQuery(id+"F3.opExtrude","CAP_EDGE",EDGE,{"disambiguationData":[OSD([sQuery(id+"F2.wireOp",EDGE,"E13.2.0")])],"isStart":false});
            var Q57;
            Q57=makeQuery(id+"F3.opExtrude","CAP_EDGE",EDGE,{"disambiguationData":[OSD([sQuery(id+"F2.wireOp",EDGE,"E13.2.2")])],"isStart":false});
            var Q58;
            {var subQ0=sQuery(id+"F2.wireOp",EDGE,"E0");Q58=makeQuery(id+"F3.opExtrude","CAP_EDGE",EDGE,{"disambiguationData":[OSD([subQ0]),TDD([makeQuery(id+"F2.imprint","IMPRINT",EDGE,{"disambiguationData":[TD([[makeQuery(id+"F2.imprint","INTERSECT",VERTEX,{"derivedFrom":[subQ0,sQuery(id+"F2.wireOp",EDGE,"E13.2.2")]}),-1.0]])],"derivedFrom":subQ0})])],"isStart":false});}
            var Q59;
            Q59=makeQuery(id+"F3.opExtrude","CAP_EDGE",EDGE,{"disambiguationData":[OSD([sQuery(id+"F2.wireOp",EDGE,"E13.3.0")])],"isStart":false});
            var Q60;
            Q60=makeQuery(id+"F3.opExtrude","CAP_EDGE",EDGE,{"disambiguationData":[OSD([sQuery(id+"F2.wireOp",EDGE,"E13.3.2")])],"isStart":false});
            var Q61;
            {var subQ0=sQuery(id+"F2.wireOp",EDGE,"E0");Q61=makeQuery(id+"F3.opExtrude","CAP_EDGE",EDGE,{"disambiguationData":[OSD([subQ0]),TDD([makeQuery(id+"F2.imprint","IMPRINT",EDGE,{"disambiguationData":[TD([[makeQuery(id+"F2.imprint","INTERSECT",VERTEX,{"derivedFrom":[subQ0,sQuery(id+"F2.wireOp",EDGE,"E13.3.2")]}),-1.0]])],"derivedFrom":subQ0})])],"isStart":false});}
            var Q62;
            Q62=makeQuery(id+"F3.opExtrude","CAP_EDGE",EDGE,{"disambiguationData":[OSD([sQuery(id+"F2.wireOp",EDGE,"E13.4.0")])],"isStart":false});
            var Q63;
            Q63=makeQuery(id+"F3.opExtrude","CAP_EDGE",EDGE,{"disambiguationData":[OSD([sQuery(id+"F2.wireOp",EDGE,"E13.4.2")])],"isStart":false});
            var Q64;
            {var subQ0=sQuery(id+"F2.wireOp",EDGE,"E0");Q64=makeQuery(id+"F3.opExtrude","CAP_EDGE",EDGE,{"disambiguationData":[OSD([subQ0]),TDD([makeQuery(id+"F2.imprint","IMPRINT",EDGE,{"disambiguationData":[TD([[makeQuery(id+"F2.imprint","INTERSECT",VERTEX,{"derivedFrom":[subQ0,sQuery(id+"F2.wireOp",EDGE,"E13.4.2")]}),-1.0]])],"derivedFrom":subQ0})])],"isStart":false});}
            var Q65;
            {var subQ0=sQuery(id+"F2.wireOp",EDGE,"E0");Q65=makeQuery(id+"F3.opExtrude","CAP_EDGE",EDGE,{"disambiguationData":[OSD([subQ0]),TDD([makeQuery(id+"F2.imprint","IMPRINT",EDGE,{"disambiguationData":[TD([[makeQuery(id+"F2.imprint","INTERSECT",VERTEX,{"derivedFrom":[subQ0,sQuery(id+"F2.wireOp",EDGE,"E13.5.2")]}),-1.0]])],"derivedFrom":subQ0})])],"isStart":true});}
            var Q66;
            Q66=makeQuery(id+"F3.opExtrude","CAP_EDGE",EDGE,{"disambiguationData":[OSD([sQuery(id+"F2.wireOp",EDGE,"E13.5.2")])],"isStart":true});
            var Q67;
            {var subQ0=sQuery(id+"F2.wireOp",EDGE,"E0");Q67=makeQuery(id+"F3.opExtrude","CAP_EDGE",EDGE,{"disambiguationData":[OSD([subQ0]),TDD([makeQuery(id+"F2.imprint","IMPRINT",EDGE,{"disambiguationData":[TD([[makeQuery(id+"F2.imprint","INTERSECT",VERTEX,{"derivedFrom":[subQ0,sQuery(id+"F2.wireOp",EDGE,"E13.4.2")]}),-1.0]])],"derivedFrom":subQ0})])],"isStart":true});}
            var Q68;
            Q68=makeQuery(id+"F3.opExtrude","CAP_EDGE",EDGE,{"disambiguationData":[OSD([sQuery(id+"F2.wireOp",EDGE,"E13.4.2")])],"isStart":true});
            var Q69;
            Q69=makeQuery(id+"F3.opExtrude","CAP_EDGE",EDGE,{"disambiguationData":[OSD([sQuery(id+"F2.wireOp",EDGE,"E13.4.0")])],"isStart":true});
            var Q70;
            {var subQ0=sQuery(id+"F2.wireOp",EDGE,"E0");Q70=makeQuery(id+"F3.opExtrude","CAP_EDGE",EDGE,{"disambiguationData":[OSD([subQ0]),TDD([makeQuery(id+"F2.imprint","IMPRINT",EDGE,{"disambiguationData":[TD([[makeQuery(id+"F2.imprint","INTERSECT",VERTEX,{"derivedFrom":[subQ0,sQuery(id+"F2.wireOp",EDGE,"E13.3.2")]}),-1.0]])],"derivedFrom":subQ0})])],"isStart":true});}
            var Q71;
            Q71=makeQuery(id+"F3.opExtrude","CAP_EDGE",EDGE,{"disambiguationData":[OSD([sQuery(id+"F2.wireOp",EDGE,"E13.3.2")])],"isStart":true});
            var Q72;
            Q72=makeQuery(id+"F3.opExtrude","CAP_EDGE",EDGE,{"disambiguationData":[OSD([sQuery(id+"F2.wireOp",EDGE,"E13.3.0")])],"isStart":true});
            var Q73;
            {var subQ0=sQuery(id+"F2.wireOp",EDGE,"E0");Q73=makeQuery(id+"F3.opExtrude","CAP_EDGE",EDGE,{"disambiguationData":[OSD([subQ0]),TDD([makeQuery(id+"F2.imprint","IMPRINT",EDGE,{"disambiguationData":[TD([[makeQuery(id+"F2.imprint","INTERSECT",VERTEX,{"derivedFrom":[subQ0,sQuery(id+"F2.wireOp",EDGE,"E13.2.2")]}),-1.0]])],"derivedFrom":subQ0})])],"isStart":true});}
            var Q74;
            Q74=makeQuery(id+"F3.opExtrude","CAP_EDGE",EDGE,{"disambiguationData":[OSD([sQuery(id+"F2.wireOp",EDGE,"E13.2.2")])],"isStart":true});
            var Q75;
            Q75=makeQuery(id+"F3.opExtrude","CAP_EDGE",EDGE,{"disambiguationData":[OSD([sQuery(id+"F2.wireOp",EDGE,"E13.2.0")])],"isStart":true});
            var Q76;
            Q76=makeQuery(id+"F3.opExtrude","CAP_EDGE",EDGE,{"disambiguationData":[OSD([sQuery(id+"F2.wireOp",EDGE,"E13.1.2")])],"isStart":true});
            var Q77;
            {var subQ0=sQuery(id+"F2.wireOp",EDGE,"E0");Q77=makeQuery(id+"F3.opExtrude","CAP_EDGE",EDGE,{"disambiguationData":[OSD([subQ0]),TDD([makeQuery(id+"F2.imprint","IMPRINT",EDGE,{"disambiguationData":[TD([[makeQuery(id+"F2.imprint","INTERSECT",VERTEX,{"derivedFrom":[subQ0,sQuery(id+"F2.wireOp",EDGE,"E13.1.2")]}),-1.0]])],"derivedFrom":subQ0})])],"isStart":true});}
            var Q78;
            Q78=makeQuery(id+"F3.opExtrude","CAP_EDGE",EDGE,{"disambiguationData":[OSD([sQuery(id+"F2.wireOp",EDGE,"E13.1.0")])],"isStart":true});
            var Q79;
            {var subQ0=sQuery(id+"F2.wireOp",EDGE,"E0");Q79=makeQuery(id+"F3.opExtrude","CAP_EDGE",EDGE,{"disambiguationData":[OSD([subQ0]),TDD([makeQuery(id+"F2.imprint","IMPRINT",EDGE,{"disambiguationData":[TD([[makeQuery(id+"F2.imprint","INTERSECT",VERTEX,{"derivedFrom":[subQ0,sQuery(id+"F2.wireOp",EDGE,"E11.MirrorCS")]}),-1.0]])],"derivedFrom":subQ0})])],"isStart":true});}
            var Q80;
            Q80=makeQuery(id+"F3.opExtrude","CAP_EDGE",EDGE,{"disambiguationData":[OSD([sQuery(id+"F2.wireOp",EDGE,"E11.MirrorCS")])],"isStart":true});
            var Q81;
            Q81=makeQuery(id+"F3.opExtrude","CAP_EDGE",EDGE,{"disambiguationData":[OSD([sQuery(id+"F2.wireOp",EDGE,"E10.trimOffspring")])],"isStart":true});
            var Q82;
            {var subQ0=sQuery(id+"F2.wireOp",EDGE,"E0");Q82=makeQuery(id+"F3.opExtrude","CAP_EDGE",EDGE,{"disambiguationData":[OSD([subQ0]),TDD([makeQuery(id+"F2.imprint","IMPRINT",EDGE,{"disambiguationData":[TD([[makeQuery(id+"F2.imprint","INTERSECT",VERTEX,{"derivedFrom":[subQ0,sQuery(id+"F2.wireOp",EDGE,"E10.trimOffspring")]}),1.0]])],"derivedFrom":subQ0})])],"isStart":true});}
            var Q83;
            Q83=makeQuery(id+"F3.opExtrude","CAP_EDGE",EDGE,{"disambiguationData":[OSD([sQuery(id+"F2.wireOp",EDGE,"E13.19.2")])],"isStart":true});
            var Q84;
            Q84=makeQuery(id+"F3.opExtrude","CAP_EDGE",EDGE,{"disambiguationData":[OSD([sQuery(id+"F2.wireOp",EDGE,"E13.19.0")])],"isStart":true});
            var Q85;
            {var subQ0=sQuery(id+"F2.wireOp",EDGE,"E0");Q85=makeQuery(id+"F3.opExtrude","CAP_EDGE",EDGE,{"disambiguationData":[OSD([subQ0]),TDD([makeQuery(id+"F2.imprint","IMPRINT",EDGE,{"disambiguationData":[TD([[makeQuery(id+"F2.imprint","INTERSECT",VERTEX,{"derivedFrom":[subQ0,sQuery(id+"F2.wireOp",EDGE,"E13.18.2")]}),-1.0]])],"derivedFrom":subQ0})])],"isStart":true});}
            var Q86;
            Q86=makeQuery(id+"F3.opExtrude","CAP_EDGE",EDGE,{"disambiguationData":[OSD([sQuery(id+"F2.wireOp",EDGE,"E13.18.2")])],"isStart":true});
            var Q87;
            Q87=makeQuery(id+"F3.opExtrude","CAP_EDGE",EDGE,{"disambiguationData":[OSD([sQuery(id+"F2.wireOp",EDGE,"E13.18.0")])],"isStart":true});
            var Q88;
            {var subQ0=sQuery(id+"F2.wireOp",EDGE,"E0");Q88=makeQuery(id+"F3.opExtrude","CAP_EDGE",EDGE,{"disambiguationData":[OSD([subQ0]),TDD([makeQuery(id+"F2.imprint","IMPRINT",EDGE,{"disambiguationData":[TD([[makeQuery(id+"F2.imprint","INTERSECT",VERTEX,{"derivedFrom":[subQ0,sQuery(id+"F2.wireOp",EDGE,"E13.17.2")]}),-1.0]])],"derivedFrom":subQ0})])],"isStart":true});}
            var Q89;
            Q89=makeQuery(id+"F3.opExtrude","CAP_EDGE",EDGE,{"disambiguationData":[OSD([sQuery(id+"F2.wireOp",EDGE,"E13.17.2")])],"isStart":true});
            var Q90;
            Q90=makeQuery(id+"F3.opExtrude","CAP_EDGE",EDGE,{"disambiguationData":[OSD([sQuery(id+"F2.wireOp",EDGE,"E13.17.0")])],"isStart":true});
            var Q91;
            {var subQ0=sQuery(id+"F2.wireOp",EDGE,"E0");Q91=makeQuery(id+"F3.opExtrude","CAP_EDGE",EDGE,{"disambiguationData":[OSD([subQ0]),TDD([makeQuery(id+"F2.imprint","IMPRINT",EDGE,{"disambiguationData":[TD([[makeQuery(id+"F2.imprint","INTERSECT",VERTEX,{"derivedFrom":[subQ0,sQuery(id+"F2.wireOp",EDGE,"E13.16.2")]}),-1.0]])],"derivedFrom":subQ0})])],"isStart":true});}
            var Q92;
            Q92=makeQuery(id+"F3.opExtrude","CAP_EDGE",EDGE,{"disambiguationData":[OSD([sQuery(id+"F2.wireOp",EDGE,"E13.16.2")])],"isStart":true});
            var Q93;
            Q93=makeQuery(id+"F3.opExtrude","CAP_EDGE",EDGE,{"disambiguationData":[OSD([sQuery(id+"F2.wireOp",EDGE,"E13.16.0")])],"isStart":true});
            var Q94;
            {var subQ0=sQuery(id+"F2.wireOp",EDGE,"E0");Q94=makeQuery(id+"F3.opExtrude","CAP_EDGE",EDGE,{"disambiguationData":[OSD([subQ0]),TDD([makeQuery(id+"F2.imprint","IMPRINT",EDGE,{"disambiguationData":[TD([[makeQuery(id+"F2.imprint","INTERSECT",VERTEX,{"derivedFrom":[subQ0,sQuery(id+"F2.wireOp",EDGE,"E13.15.2")]}),-1.0]])],"derivedFrom":subQ0})])],"isStart":true});}
            var Q95;
            Q95=makeQuery(id+"F3.opExtrude","CAP_EDGE",EDGE,{"disambiguationData":[OSD([sQuery(id+"F2.wireOp",EDGE,"E13.15.2")])],"isStart":true});
            var Q96;
            Q96=makeQuery(id+"F3.opExtrude","CAP_EDGE",EDGE,{"disambiguationData":[OSD([sQuery(id+"F2.wireOp",EDGE,"E13.15.0")])],"isStart":true});
            var Q97;
            {var subQ0=sQuery(id+"F2.wireOp",EDGE,"E0");Q97=makeQuery(id+"F3.opExtrude","CAP_EDGE",EDGE,{"disambiguationData":[OSD([subQ0]),TDD([makeQuery(id+"F2.imprint","IMPRINT",EDGE,{"disambiguationData":[TD([[makeQuery(id+"F2.imprint","INTERSECT",VERTEX,{"derivedFrom":[subQ0,sQuery(id+"F2.wireOp",EDGE,"E13.14.2")]}),-1.0]])],"derivedFrom":subQ0})])],"isStart":true});}
            var Q98;
            Q98=makeQuery(id+"F3.opExtrude","CAP_EDGE",EDGE,{"disambiguationData":[OSD([sQuery(id+"F2.wireOp",EDGE,"E13.14.2")])],"isStart":true});
            var Q99;
            Q99=makeQuery(id+"F3.opExtrude","CAP_EDGE",EDGE,{"disambiguationData":[OSD([sQuery(id+"F2.wireOp",EDGE,"E13.14.0")])],"isStart":true});
            var Q100;
            {var subQ0=sQuery(id+"F2.wireOp",EDGE,"E0");Q100=makeQuery(id+"F3.opExtrude","CAP_EDGE",EDGE,{"disambiguationData":[OSD([subQ0]),TDD([makeQuery(id+"F2.imprint","IMPRINT",EDGE,{"disambiguationData":[TD([[makeQuery(id+"F2.imprint","INTERSECT",VERTEX,{"derivedFrom":[subQ0,sQuery(id+"F2.wireOp",EDGE,"E13.13.2")]}),-1.0]])],"derivedFrom":subQ0})])],"isStart":true});}
            var Q101;
            Q101=makeQuery(id+"F3.opExtrude","CAP_EDGE",EDGE,{"disambiguationData":[OSD([sQuery(id+"F2.wireOp",EDGE,"E13.13.2")])],"isStart":true});
            var Q102;
            Q102=makeQuery(id+"F3.opExtrude","CAP_EDGE",EDGE,{"disambiguationData":[OSD([sQuery(id+"F2.wireOp",EDGE,"E13.13.0")])],"isStart":true});
            var Q103;
            {var subQ0=sQuery(id+"F2.wireOp",EDGE,"E0");Q103=makeQuery(id+"F3.opExtrude","CAP_EDGE",EDGE,{"disambiguationData":[OSD([subQ0]),TDD([makeQuery(id+"F2.imprint","IMPRINT",EDGE,{"disambiguationData":[TD([[makeQuery(id+"F2.imprint","INTERSECT",VERTEX,{"derivedFrom":[subQ0,sQuery(id+"F2.wireOp",EDGE,"E13.12.2")]}),-1.0]])],"derivedFrom":subQ0})])],"isStart":true});}
            var Q104;
            Q104=makeQuery(id+"F3.opExtrude","CAP_EDGE",EDGE,{"disambiguationData":[OSD([sQuery(id+"F2.wireOp",EDGE,"E13.12.2")])],"isStart":true});
            var Q105;
            Q105=makeQuery(id+"F3.opExtrude","CAP_EDGE",EDGE,{"disambiguationData":[OSD([sQuery(id+"F2.wireOp",EDGE,"E13.12.0")])],"isStart":true});
            var Q106;
            {var subQ0=sQuery(id+"F2.wireOp",EDGE,"E0");Q106=makeQuery(id+"F3.opExtrude","CAP_EDGE",EDGE,{"disambiguationData":[OSD([subQ0]),TDD([makeQuery(id+"F2.imprint","IMPRINT",EDGE,{"disambiguationData":[TD([[makeQuery(id+"F2.imprint","INTERSECT",VERTEX,{"derivedFrom":[subQ0,sQuery(id+"F2.wireOp",EDGE,"E13.11.2")]}),-1.0]])],"derivedFrom":subQ0})])],"isStart":true});}
            var Q107;
            Q107=makeQuery(id+"F3.opExtrude","CAP_EDGE",EDGE,{"disambiguationData":[OSD([sQuery(id+"F2.wireOp",EDGE,"E13.11.2")])],"isStart":true});
            var Q108;
            Q108=makeQuery(id+"F3.opExtrude","CAP_EDGE",EDGE,{"disambiguationData":[OSD([sQuery(id+"F2.wireOp",EDGE,"E13.11.0")])],"isStart":true});
            var Q109;
            {var subQ0=sQuery(id+"F2.wireOp",EDGE,"E0");Q109=makeQuery(id+"F3.opExtrude","CAP_EDGE",EDGE,{"disambiguationData":[OSD([subQ0]),TDD([makeQuery(id+"F2.imprint","IMPRINT",EDGE,{"disambiguationData":[TD([[makeQuery(id+"F2.imprint","INTERSECT",VERTEX,{"derivedFrom":[subQ0,sQuery(id+"F2.wireOp",EDGE,"E13.10.2")]}),-1.0]])],"derivedFrom":subQ0})])],"isStart":true});}
            var Q110;
            Q110=makeQuery(id+"F3.opExtrude","CAP_EDGE",EDGE,{"disambiguationData":[OSD([sQuery(id+"F2.wireOp",EDGE,"E13.10.2")])],"isStart":true});
            var Q111;
            Q111=makeQuery(id+"F3.opExtrude","CAP_EDGE",EDGE,{"disambiguationData":[OSD([sQuery(id+"F2.wireOp",EDGE,"E13.10.0")])],"isStart":true});
            var Q112;
            {var subQ0=sQuery(id+"F2.wireOp",EDGE,"E0");Q112=makeQuery(id+"F3.opExtrude","CAP_EDGE",EDGE,{"disambiguationData":[OSD([subQ0]),TDD([makeQuery(id+"F2.imprint","IMPRINT",EDGE,{"disambiguationData":[TD([[makeQuery(id+"F2.imprint","INTERSECT",VERTEX,{"derivedFrom":[subQ0,sQuery(id+"F2.wireOp",EDGE,"E13.9.2")]}),-1.0]])],"derivedFrom":subQ0})])],"isStart":true});}
            var Q113;
            Q113=makeQuery(id+"F3.opExtrude","CAP_EDGE",EDGE,{"disambiguationData":[OSD([sQuery(id+"F2.wireOp",EDGE,"E13.9.2")])],"isStart":true});
            var Q114;
            Q114=makeQuery(id+"F3.opExtrude","CAP_EDGE",EDGE,{"disambiguationData":[OSD([sQuery(id+"F2.wireOp",EDGE,"E13.9.0")])],"isStart":true});
            var Q115;
            {var subQ0=sQuery(id+"F2.wireOp",EDGE,"E0");Q115=makeQuery(id+"F3.opExtrude","CAP_EDGE",EDGE,{"disambiguationData":[OSD([subQ0]),TDD([makeQuery(id+"F2.imprint","IMPRINT",EDGE,{"disambiguationData":[TD([[makeQuery(id+"F2.imprint","INTERSECT",VERTEX,{"derivedFrom":[subQ0,sQuery(id+"F2.wireOp",EDGE,"E13.8.2")]}),-1.0]])],"derivedFrom":subQ0})])],"isStart":true});}
            var Q116;
            Q116=makeQuery(id+"F3.opExtrude","CAP_EDGE",EDGE,{"disambiguationData":[OSD([sQuery(id+"F2.wireOp",EDGE,"E13.8.2")])],"isStart":true});
            fillet(context, id + "F4", {"entities" : qUnion([Q0, Q1, Q2, Q3, Q4, Q5, Q6, Q7, Q8, Q9, Q10, Q11, Q12, Q13, Q14, Q15, Q16, Q17, Q18, Q19, Q20, Q21, Q22, Q23, Q24, Q25, Q26, Q27, Q28, Q29, Q30, Q31, Q32, Q33, Q34, Q35, Q36, Q37, Q38, Q39, Q40, Q41, Q42, Q43, Q44, Q45, Q46, Q47, Q48, Q49, Q50, Q51, Q52, Q53, Q54, Q55, Q56, Q57, Q58, Q59, Q60, Q61, Q62, Q63, Q64, Q65, Q66, Q67, Q68, Q69, Q70, Q71, Q72, Q73, Q74, Q75, Q76, Q77, Q78, Q79, Q80, Q81, Q82, Q83, Q84, Q85, Q86, Q87, Q88, Q89, Q90, Q91, Q92, Q93, Q94, Q95, Q96, Q97, Q98, Q99, Q100, Q101, Q102, Q103, Q104, Q105, Q106, Q107, Q108, Q109, Q110, Q111, Q112, Q113, Q114, Q115, Q116]), "radius" : (getVariable(context, 'TeethFillet')) * mm, "tangentPropagation" : true, "allowEdgeOverflow" : false});
        }
    });
